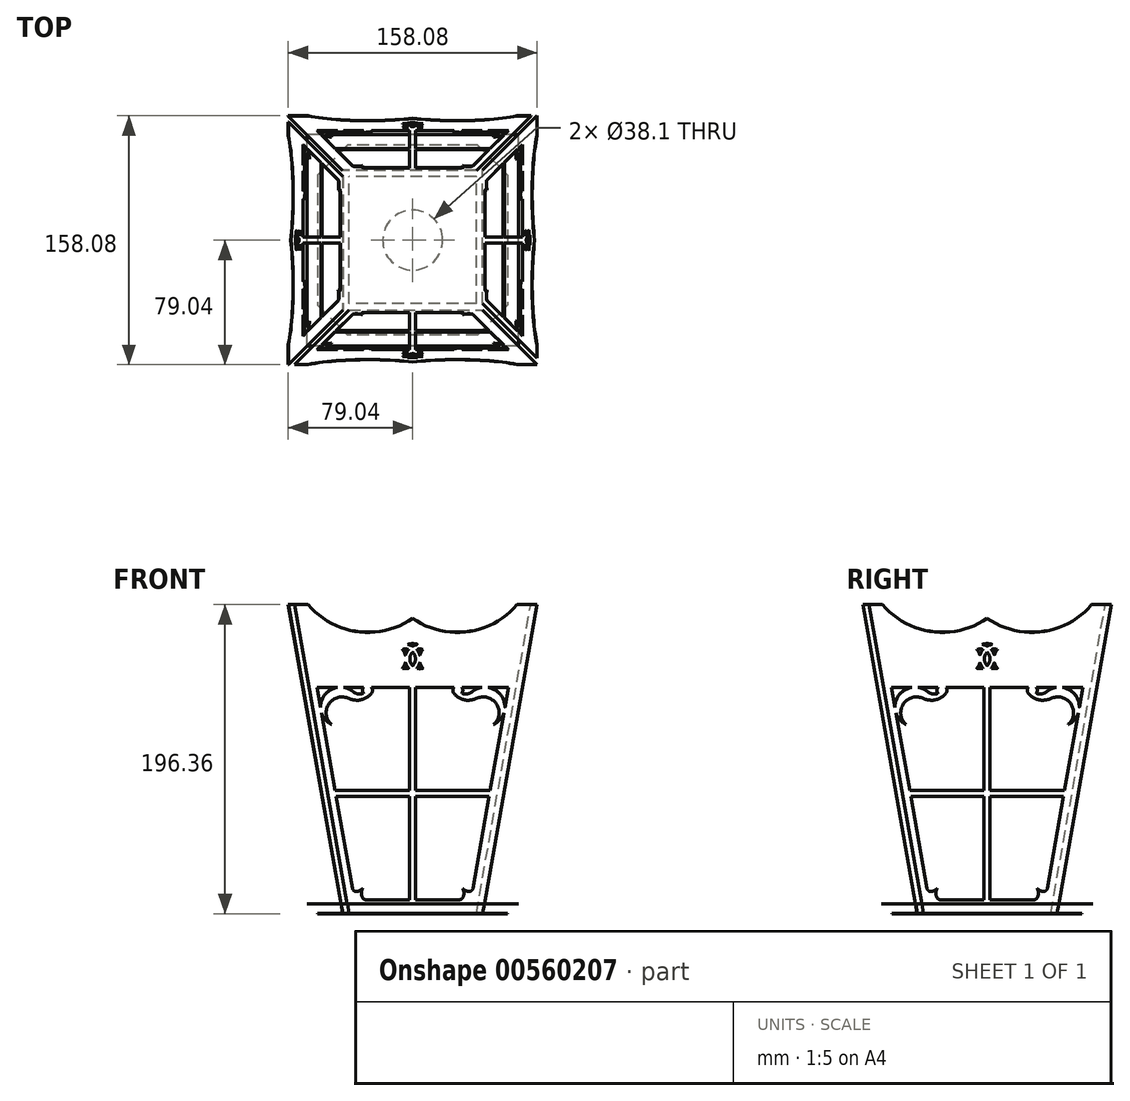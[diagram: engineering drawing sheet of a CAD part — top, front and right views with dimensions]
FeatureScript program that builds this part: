
annotation { "Feature Type Name" : "Feature", "Feature Type Description" : "" }
export const myFeature = defineFeature(function(context is Context, id is Id, definition is map)
    precondition{}
    {
        {
            assignVariable(context, id + "F0", {"name" : "wood_thickness", "anyValue" : 5 / 32});
        }
        {
            var Q0;
            Q0=qCreatedBy(makeId("Top.planeOp"),FACE);
            var sketch = newSketch(context, id + "F1", { "sketchPlane" : qUnion([Q0])});
            skLineSegment(sketch, "E0.bottom", {"start": v(41.27, 60.33) * mm, "end": v(-41.28, 60.33) * mm});
            skLineSegment(sketch, "E0.top", {"start": v(41.28, -60.32) * mm, "end": v(-41.28, -60.32) * mm});
            skLineSegment(sketch, "E0.left", {"start": v(60.32, 41.28) * mm, "end": v(60.32, -41.27) * mm});
            skLineSegment(sketch, "E0.right", {"start": v(-60.32, 41.28) * mm, "end": v(-60.32, -41.27) * mm});
            skPoint(sketch, "E0.middle", {"position": v(0, 0) * mm});
            skLineSegment(sketch, "E1", {"start": v(-41.28, 60.33) * mm, "end": v(-60.33, 41.28) * mm});
            skLineSegment(sketch, "E2", {"start": v(-60.33, -41.28) * mm, "end": v(-41.27, -60.33) * mm});
            skLineSegment(sketch, "E3", {"start": v(41.28, -60.32) * mm, "end": v(60.33, -41.27) * mm});
            skLineSegment(sketch, "E4", {"start": v(41.27, 60.33) * mm, "end": v(60.33, 41.28) * mm});
            skPoint(sketch, "E5.orphan", {"position": v(-60.32, 60.32) * mm});
            skPoint(sketch, "E6.orphan", {"position": v(60.32, 60.32) * mm});
            skPoint(sketch, "E7.orphan", {"position": v(60.32, -60.32) * mm});
            skPoint(sketch, "E8.orphan", {"position": v(-60.32, -60.32) * mm});
            skCircle(sketch, "E9", {"center": v(0, 0) * mm, "radius": 19.05 * mm});
            skLineSegment(sketch, "E10.bottom", {"start": v(44.45, -44.45) * mm, "end": v(-44.45, -44.45) * mm, "construction": true});
            skLineSegment(sketch, "E10.top", {"start": v(44.45, 44.45) * mm, "end": v(-44.45, 44.45) * mm, "construction": true});
            skLineSegment(sketch, "E10.left", {"start": v(44.45, 44.45) * mm, "end": v(44.45, -44.45) * mm, "construction": true});
            skLineSegment(sketch, "E10.right", {"start": v(-44.45, 44.45) * mm, "end": v(-44.45, -44.45) * mm, "construction": true});
            skCircle(sketch, "E11", {"center": v(0, 0) * mm, "radius": 50.8 * mm, "construction": true});
            skSolve(sketch);
        }
        {
            var Q0;
            Q0=makeQuery(id+"F1.imprint","IMPRINT",FACE,{"disambiguationData":[TD([[makeQuery(id+"F1.imprint","IMPRINT",EDGE,{"derivedFrom":sQuery(id+"F1.wireOp",EDGE,"E0.bottom")}),1.0]])]});
            extrude(context, id + "F2", {"entities" : qUnion([Q0]), "oppositeDirection" : true, "depth" : (getVariable(context, 'wood_thickness')) * mm, "offsetDistance" : 25.4 * mm});
        }
        {
            assignVariable(context, id + "F3", {"name" : "angle", "anyValue" : 10});
        }
        {
            assignVariable(context, id + "F4", {"name" : "window_height", "anyValue" : 6});
        }
        {
            var Q0;
            Q0=sQuery(id+"F1.wireOp",EDGE,"E10.bottom");
            var Q1;
            Q1=qCreatedBy(makeId("Front.planeOp"),FACE);
            cPlane(context, id + "F5", {"entities" : qUnion([Q0, Q1]), "cplaneType" : CPlaneType.LINE_ANGLE, "offset" : 25.4 * mm, "angle" : 10 * degree, "oppositeDirection" : true, "width" : 152.4 * mm, "height" : 152.4 * mm});
        }
        {
            var Q0;
            Q0=sQuery(id+"F1.wireOp",EDGE,"E10.left");
            var Q1;
            Q1=qCreatedBy(makeId("Right.planeOp"),FACE);
            cPlane(context, id + "F6", {"entities" : qUnion([Q0, Q1]), "cplaneType" : CPlaneType.LINE_ANGLE, "offset" : 25.4 * mm, "angle" : (getVariable(context, 'angle')) * degree, "oppositeDirection" : true, "width" : 152.4 * mm, "height" : 152.4 * mm});
        }
        {
            var Q0;
            Q0=qCreatedBy(makeId("Top.planeOp"),FACE);
            cPlane(context, id + "F7", {"entities" : qUnion([Q0]), "cplaneType" : CPlaneType.OFFSET, "offset" : (getVariable(context, 'window_height')) * mm, "width" : 152.4 * mm, "height" : 152.4 * mm});
        }
        {
            var Q0;
            Q0=qCreatedBy(id+"F5.planeOp",FACE);
            var sketch = newSketch(context, id + "F8", { "sketchPlane" : qUnion([Q0])});
            skLineSegment(sketch, "E12", {"start": v(44.45, 7.72) * mm, "end": v(71.32, 162.47) * mm, "construction": true});
            skLineSegment(sketch, "E13", {"start": v(71.32, 162.47) * mm, "end": v(-71.32, 162.47) * mm, "construction": true});
            skLineSegment(sketch, "E14", {"start": v(-71.32, 162.47) * mm, "end": v(-44.45, 7.72) * mm, "construction": true});
            skLineSegment(sketch, "E15", {"start": v(-44.45, 7.72) * mm, "end": v(44.45, 7.72) * mm, "construction": true});
            skPoint(sketch, "E16", {"position": v(0, 162.47) * mm});
            skPoint(sketch, "E17", {"position": v(0, 7.72) * mm});
            skLineSegment(sketch, "E18", {"start": v(40.42, 7.72) * mm, "end": v(75.01, 206.92) * mm});
            skLineSegment(sketch, "E19", {"start": v(40.42, 7.72) * mm, "end": v(-44.45, 7.72) * mm});
            skLineSegment(sketch, "E20", {"start": v(-44.45, 7.72) * mm, "end": v(-79.04, 206.92) * mm});
            skLineSegment(sketch, "E21", {"start": v(71.32, 162.47) * mm, "end": v(79.04, 206.92) * mm, "construction": true});
            skLineSegment(sketch, "E22", {"start": v(74.63, 181.52) * mm, "end": v(-74.63, 181.52) * mm, "construction": true});
            skLineSegment(sketch, "E23", {"start": v(79.04, 206.92) * mm, "end": v(66.34, 206.92) * mm, "construction": true});
            skLineSegment(sketch, "E24", {"start": v(-79.04, 206.92) * mm, "end": v(-66.34, 206.92) * mm});
            skArc(sketch, "E25", {"start": v(0, 198.03) * mm, "mid": v(34.9, 189.58) * mm, "end": v(66.34, 206.92) * mm});
            skArc(sketch, "E26", {"start": v(-66.34, 206.92) * mm, "mid": v(-34.9, 189.58) * mm, "end": v(0, 198.03) * mm});
            skLineSegment(sketch, "E27", {"start": v(75.01, 206.92) * mm, "end": v(66.34, 206.92) * mm});
            skLineSegment(sketch, "E28", {"start": v(79.04, 206.92) * mm, "end": v(74.1, 207.78) * mm, "construction": true});
            skLineSegment(sketch, "E29", {"start": v(29.6, 16.6) * mm, "end": v(1.9, 16.6) * mm});
            skPoint(sketch, "E30", {"position": v(0, 16.6) * mm});
            skLineSegment(sketch, "E31", {"start": v(-60.76, 153.58) * mm, "end": v(-47.74, 153.58) * mm});
            skLineSegment(sketch, "E32", {"start": v(60.76, 153.58) * mm, "end": v(58.53, 140.75) * mm});
            skLineSegment(sketch, "E33", {"start": v(60.76, 153.58) * mm, "end": v(-36.97, 16.6) * mm, "construction": true});
            skLineSegment(sketch, "E34", {"start": v(-60.76, 153.58) * mm, "end": v(36.97, 16.6) * mm, "construction": true});
            skLineSegment(sketch, "E35", {"start": v(0, 153.58) * mm, "end": v(0, 16.6) * mm, "construction": true});
            skLineSegment(sketch, "E36", {"start": v(48.86, 85.1) * mm, "end": v(-48.86, 85.1) * mm, "construction": true});
            skArc(sketch, "E37", {"start": v(-31.87, 18) * mm, "mid": v(-30.94, 16.99) * mm, "end": v(-29.6, 16.6) * mm});
            skArc(sketch, "E38", {"start": v(-31.8, 23.85) * mm, "mid": v(-32.55, 20.93) * mm, "end": v(-31.87, 18) * mm});
            skLineSegment(sketch, "E39", {"start": v(-31.8, 23.85) * mm, "end": v(-35.66, 16.6) * mm, "construction": true});
            skArc(sketch, "E40", {"start": v(-35.28, 21.93) * mm, "mid": v(-33.4, 22.61) * mm, "end": v(-31.8, 23.85) * mm});
            skLineSegment(sketch, "E41", {"start": v(-31.8, 23.85) * mm, "end": v(-37.22, 18.04) * mm, "construction": true});
            skArc(sketch, "E42", {"start": v(-38.25, 24) * mm, "mid": v(-37.2, 22.35) * mm, "end": v(-35.28, 21.93) * mm});
            skLineSegment(sketch, "E43.trimOffspring", {"start": v(-38.25, 24) * mm, "end": v(-48.53, 83.19) * mm});
            skArc(sketch, "E44", {"start": v(29.6, 16.6) * mm, "mid": v(30.94, 16.99) * mm, "end": v(31.87, 18) * mm});
            skArc(sketch, "E45", {"start": v(31.87, 18) * mm, "mid": v(32.55, 20.93) * mm, "end": v(31.8, 23.85) * mm});
            skArc(sketch, "E46", {"start": v(31.8, 23.85) * mm, "mid": v(33.4, 22.61) * mm, "end": v(35.28, 21.93) * mm});
            skArc(sketch, "E47", {"start": v(35.28, 21.93) * mm, "mid": v(37.2, 22.35) * mm, "end": v(38.25, 24) * mm});
            skLineSegment(sketch, "E48", {"start": v(31.8, 23.85) * mm, "end": v(34.55, 18.69) * mm, "construction": true});
            skLineSegment(sketch, "E49", {"start": v(31.8, 23.85) * mm, "end": v(35.1, 20.32) * mm, "construction": true});
            skLineSegment(sketch, "E50", {"start": v(1.9, 153.58) * mm, "end": v(1.9, 87) * mm});
            skLineSegment(sketch, "E51", {"start": v(-1.9, 153.58) * mm, "end": v(-1.9, 87) * mm});
            skLineSegment(sketch, "E52", {"start": v(1.9, 112.49) * mm, "end": v(-1.9, 112.49) * mm, "construction": true});
            skPoint(sketch, "E53", {"position": v(0, 112.49) * mm});
            skLineSegment(sketch, "E54", {"start": v(49.2, 87) * mm, "end": v(1.9, 87) * mm});
            skLineSegment(sketch, "E55", {"start": v(-48.53, 83.19) * mm, "end": v(-1.9, 83.19) * mm});
            skLineSegment(sketch, "E56", {"start": v(26.8, 87) * mm, "end": v(26.8, 83.19) * mm, "construction": true});
            skPoint(sketch, "E57", {"position": v(26.8, 85.1) * mm});
            skLineSegment(sketch, "E58", {"start": v(60.76, 153.58) * mm, "end": v(0, 102.47) * mm, "construction": true});
            skLineSegment(sketch, "E59", {"start": v(0, 102.47) * mm, "end": v(-60.76, 153.58) * mm, "construction": true});
            skLineSegment(sketch, "E60", {"start": v(-37.33, 153.58) * mm, "end": v(-56.75, 130.5) * mm, "construction": true});
            skPoint(sketch, "E61", {"position": v(-47.04, 142.04) * mm});
            skArc(sketch, "E62", {"start": v(51.47, 129.65) * mm, "mid": v(55.4, 132.68) * mm, "end": v(57.88, 137) * mm});
            skPoint(sketch, "E63", {"position": v(47.74, 153.58) * mm});
            skPoint(sketch, "E64", {"position": v(43.93, 153.58) * mm});
            skArc(sketch, "E65", {"start": v(37.58, 150.67) * mm, "mid": v(34.53, 149.3) * mm, "end": v(31.22, 149.77) * mm});
            skArc(sketch, "E66", {"start": v(51.47, 129.65) * mm, "mid": v(53.23, 142.87) * mm, "end": v(40.38, 146.44) * mm});
            skLineSegment(sketch, "E67", {"start": v(51.47, 129.65) * mm, "end": v(37.58, 150.67) * mm, "construction": true});
            skLineSegment(sketch, "E68", {"start": v(51.47, 129.65) * mm, "end": v(48.2, 128.02) * mm, "construction": true});
            skLineSegment(sketch, "E69", {"start": v(51.47, 129.65) * mm, "end": v(49.55, 127.95) * mm, "construction": true});
            skArc(sketch, "E70", {"start": v(26.15, 153.58) * mm, "mid": v(25.51, 151.67) * mm, "end": v(26.15, 149.77) * mm});
            skArc(sketch, "E71.trimOffspring", {"start": v(26.15, 149.77) * mm, "mid": v(32.68, 145.6) * mm, "end": v(40.38, 146.44) * mm});
            skArc(sketch, "E72.trimOffspring", {"start": v(31.22, 149.77) * mm, "mid": v(31.86, 151.67) * mm, "end": v(31.22, 153.58) * mm});
            skLineSegment(sketch, "E73", {"start": v(31.22, 153.58) * mm, "end": v(26.15, 149.77) * mm, "construction": true});
            skLineSegment(sketch, "E74", {"start": v(26.15, 153.58) * mm, "end": v(31.22, 149.77) * mm, "construction": true});
            skPoint(sketch, "E75", {"position": v(58.53, 140.75) * mm});
            skPoint(sketch, "E76", {"position": v(57.88, 137) * mm});
            skArc(sketch, "E77.trimOffspring", {"start": v(58.53, 140.75) * mm, "mid": v(55.55, 149.2) * mm, "end": v(47.74, 153.58) * mm});
            skLineSegment(sketch, "E78.trimOffspring", {"start": v(57.88, 137) * mm, "end": v(49.2, 87) * mm});
            skArc(sketch, "E79.trimOffspring", {"start": v(43.93, 153.58) * mm, "mid": v(40.55, 152.57) * mm, "end": v(37.58, 150.67) * mm});
            skLineSegment(sketch, "E80.trimOffspring", {"start": v(47.74, 153.58) * mm, "end": v(60.76, 153.58) * mm});
            skArc(sketch, "E81.MirrorCS", {"start": v(-26.15, 153.58) * mm, "mid": v(-25.51, 151.67) * mm, "end": v(-26.15, 149.77) * mm});
            skArc(sketch, "E82.MirrorCS", {"start": v(-31.22, 149.77) * mm, "mid": v(-31.86, 151.67) * mm, "end": v(-31.22, 153.58) * mm});
            skArc(sketch, "E83.MirrorCS", {"start": v(-37.58, 150.67) * mm, "mid": v(-34.53, 149.3) * mm, "end": v(-31.22, 149.77) * mm});
            skArc(sketch, "E84.MirrorCS", {"start": v(-26.15, 149.77) * mm, "mid": v(-32.68, 145.6) * mm, "end": v(-40.38, 146.44) * mm});
            skArc(sketch, "E85.MirrorCS", {"start": v(-43.93, 153.58) * mm, "mid": v(-40.55, 152.57) * mm, "end": v(-37.58, 150.67) * mm});
            skArc(sketch, "E86.MirrorCS", {"start": v(-51.47, 129.65) * mm, "mid": v(-55.4, 132.68) * mm, "end": v(-57.88, 137) * mm});
            skArc(sketch, "E87.MirrorCS", {"start": v(-51.47, 129.65) * mm, "mid": v(-53.23, 142.87) * mm, "end": v(-40.38, 146.44) * mm});
            skArc(sketch, "E88.MirrorCS", {"start": v(-58.53, 140.75) * mm, "mid": v(-55.55, 149.2) * mm, "end": v(-47.74, 153.58) * mm});
            skLineSegment(sketch, "E89.trimOffspring", {"start": v(31.22, 153.58) * mm, "end": v(43.93, 153.58) * mm});
            skLineSegment(sketch, "E90.trimOffspring", {"start": v(-26.15, 153.58) * mm, "end": v(-1.9, 153.58) * mm});
            skLineSegment(sketch, "E91.trimOffspring", {"start": v(-43.93, 153.58) * mm, "end": v(-31.22, 153.58) * mm});
            skLineSegment(sketch, "E92.trimOffspring", {"start": v(-58.53, 140.75) * mm, "end": v(-60.76, 153.58) * mm});
            skLineSegment(sketch, "E93.trimOffspring", {"start": v(-1.9, 87) * mm, "end": v(-49.2, 87) * mm});
            skLineSegment(sketch, "E94.trimOffspring", {"start": v(1.9, 83.19) * mm, "end": v(1.9, 16.6) * mm});
            skLineSegment(sketch, "E95.trimOffspring", {"start": v(1.9, 83.19) * mm, "end": v(48.53, 83.19) * mm});
            skLineSegment(sketch, "E96.trimOffspring", {"start": v(-1.9, 83.19) * mm, "end": v(-1.9, 16.6) * mm});
            skLineSegment(sketch, "E97.trimOffspring", {"start": v(48.53, 83.19) * mm, "end": v(38.25, 24) * mm});
            skLineSegment(sketch, "E98.trimOffspring", {"start": v(-49.2, 87) * mm, "end": v(-57.88, 137) * mm});
            skLineSegment(sketch, "E99.trimOffspring", {"start": v(-1.9, 16.6) * mm, "end": v(-29.6, 16.6) * mm});
            skLineSegment(sketch, "E100.trimOffspring", {"start": v(1.9, 153.58) * mm, "end": v(26.15, 153.58) * mm});
            skLineSegment(sketch, "E101", {"start": v(0, 162.47) * mm, "end": v(0, 181.52) * mm, "construction": true});
            skPoint(sketch, "E102", {"position": v(0, 172) * mm});
            skArc(sketch, "E103", {"start": v(0, 180.2) * mm, "mid": v(-1.54, 180.89) * mm, "end": v(-3.17, 181.29) * mm});
            skArc(sketch, "E104", {"start": v(-2.62, 178.04) * mm, "mid": v(-3.82, 176.22) * mm, "end": v(-4.57, 174.16) * mm});
            skLineSegment(sketch, "E105", {"start": v(4.57, 172) * mm, "end": v(-4.57, 172) * mm, "construction": true});
            skArc(sketch, "E106", {"start": v(0, 176.4) * mm, "mid": v(-1.78, 172) * mm, "end": v(0, 167.59) * mm});
            skArc(sketch, "E107", {"start": v(-2.62, 178.04) * mm, "mid": v(-4.57, 178.34) * mm, "end": v(-6.52, 178.04) * mm});
            skArc(sketch, "E108", {"start": v(-4.57, 174.16) * mm, "mid": v(-5.32, 176.22) * mm, "end": v(-6.52, 178.04) * mm});
            skArc(sketch, "E109", {"start": v(6.52, 178.04) * mm, "mid": v(5.32, 176.22) * mm, "end": v(4.57, 174.16) * mm});
            skArc(sketch, "E110", {"start": v(3.18, 181.29) * mm, "mid": v(0, 181.82) * mm, "end": v(-3.17, 181.29) * mm});
            skArc(sketch, "E111.trimOffspring", {"start": v(6.52, 178.04) * mm, "mid": v(4.57, 178.34) * mm, "end": v(2.62, 178.04) * mm});
            skArc(sketch, "E112.trimOffspring", {"start": v(3.18, 181.29) * mm, "mid": v(1.54, 180.89) * mm, "end": v(0, 180.2) * mm});
            skArc(sketch, "E113.trimOffspring", {"start": v(2.62, 165.95) * mm, "mid": v(3.82, 167.77) * mm, "end": v(4.57, 169.82) * mm});
            skArc(sketch, "E114.trimOffspring", {"start": v(2.62, 165.95) * mm, "mid": v(4.57, 165.64) * mm, "end": v(6.52, 165.95) * mm});
            skArc(sketch, "E115.trimOffspring", {"start": v(4.57, 169.82) * mm, "mid": v(5.32, 167.77) * mm, "end": v(6.52, 165.95) * mm});
            skArc(sketch, "E116.trimOffspring", {"start": v(4.57, 174.16) * mm, "mid": v(3.82, 176.22) * mm, "end": v(2.62, 178.04) * mm});
            skArc(sketch, "E117.trimOffspring", {"start": v(0, 167.59) * mm, "mid": v(1.78, 172) * mm, "end": v(0, 176.4) * mm});
            skArc(sketch, "E118.trimOffspring", {"start": v(-4.57, 169.82) * mm, "mid": v(-3.82, 167.77) * mm, "end": v(-2.62, 165.95) * mm});
            skArc(sketch, "E119.trimOffspring", {"start": v(-6.52, 165.95) * mm, "mid": v(-5.32, 167.77) * mm, "end": v(-4.57, 169.82) * mm});
            skArc(sketch, "E120.trimOffspring", {"start": v(-6.52, 165.95) * mm, "mid": v(-4.57, 165.64) * mm, "end": v(-2.62, 165.95) * mm});
            skSolve(sketch);
        }
        {
            var Q0;
            Q0 = qSketchRegion(id + "F8", true);
            extrude(context, id + "F9", {"entities" : qUnion([Q0]), "depth" : (getVariable(context, 'wood_thickness')) * mm, "offsetDistance" : 25.4 * mm});
        }
        {
            var Q0;
            Q0=qCreatedBy(makeId("Front.planeOp"),FACE);
            var sketch = newSketch(context, id + "F10", { "sketchPlane" : qUnion([Q0])});
            skLineSegment(sketch, "E121", {"start": v(0, 0) * mm, "end": v(0, 130.04) * mm});
            skSolve(sketch);
        }
        {
            var Q0;
            Q0=makeQuery(id+"F9.opExtrude","SWEPT_BODY",BODY,{"disambiguationData":[OSD([sQuery(id+"F8.wireOp",EDGE,"E18"),sQuery(id+"F8.wireOp",EDGE,"E19"),sQuery(id+"F8.wireOp",EDGE,"E20"),sQuery(id+"F8.wireOp",EDGE,"E24"),sQuery(id+"F8.wireOp",EDGE,"E25"),sQuery(id+"F8.wireOp",EDGE,"E26"),sQuery(id+"F8.wireOp",EDGE,"E27"),sQuery(id+"F8.wireOp",EDGE,"E29"),sQuery(id+"F8.wireOp",EDGE,"E31"),sQuery(id+"F8.wireOp",EDGE,"E32"),sQuery(id+"F8.wireOp",EDGE,"E37"),sQuery(id+"F8.wireOp",EDGE,"E38"),sQuery(id+"F8.wireOp",EDGE,"E40"),sQuery(id+"F8.wireOp",EDGE,"E42"),sQuery(id+"F8.wireOp",EDGE,"E43.trimOffspring"),sQuery(id+"F8.wireOp",EDGE,"E44"),sQuery(id+"F8.wireOp",EDGE,"E45"),sQuery(id+"F8.wireOp",EDGE,"E46"),sQuery(id+"F8.wireOp",EDGE,"E47"),sQuery(id+"F8.wireOp",EDGE,"E50"),sQuery(id+"F8.wireOp",EDGE,"E51"),sQuery(id+"F8.wireOp",EDGE,"E54"),sQuery(id+"F8.wireOp",EDGE,"E55"),sQuery(id+"F8.wireOp",EDGE,"E62"),sQuery(id+"F8.wireOp",EDGE,"E65"),sQuery(id+"F8.wireOp",EDGE,"E66"),sQuery(id+"F8.wireOp",EDGE,"E70"),sQuery(id+"F8.wireOp",EDGE,"E71.trimOffspring"),sQuery(id+"F8.wireOp",EDGE,"E72.trimOffspring"),sQuery(id+"F8.wireOp",EDGE,"E77.trimOffspring"),sQuery(id+"F8.wireOp",EDGE,"E78.trimOffspring"),sQuery(id+"F8.wireOp",EDGE,"E79.trimOffspring"),sQuery(id+"F8.wireOp",EDGE,"E80.trimOffspring"),sQuery(id+"F8.wireOp",EDGE,"E81.MirrorCS"),sQuery(id+"F8.wireOp",EDGE,"E82.MirrorCS"),sQuery(id+"F8.wireOp",EDGE,"E83.MirrorCS"),sQuery(id+"F8.wireOp",EDGE,"E84.MirrorCS"),sQuery(id+"F8.wireOp",EDGE,"E85.MirrorCS"),sQuery(id+"F8.wireOp",EDGE,"E86.MirrorCS"),sQuery(id+"F8.wireOp",EDGE,"E87.MirrorCS"),sQuery(id+"F8.wireOp",EDGE,"E88.MirrorCS"),sQuery(id+"F8.wireOp",EDGE,"E89.trimOffspring"),sQuery(id+"F8.wireOp",EDGE,"E90.trimOffspring"),sQuery(id+"F8.wireOp",EDGE,"E91.trimOffspring"),sQuery(id+"F8.wireOp",EDGE,"E92.trimOffspring"),sQuery(id+"F8.wireOp",EDGE,"E93.trimOffspring"),sQuery(id+"F8.wireOp",EDGE,"E94.trimOffspring"),sQuery(id+"F8.wireOp",EDGE,"E95.trimOffspring"),sQuery(id+"F8.wireOp",EDGE,"E96.trimOffspring"),sQuery(id+"F8.wireOp",EDGE,"E97.trimOffspring"),sQuery(id+"F8.wireOp",EDGE,"E98.trimOffspring"),sQuery(id+"F8.wireOp",EDGE,"E99.trimOffspring"),sQuery(id+"F8.wireOp",EDGE,"E100.trimOffspring"),sQuery(id+"F8.wireOp",EDGE,"E103"),sQuery(id+"F8.wireOp",EDGE,"E104"),sQuery(id+"F8.wireOp",EDGE,"E106"),sQuery(id+"F8.wireOp",EDGE,"E107"),sQuery(id+"F8.wireOp",EDGE,"E108"),sQuery(id+"F8.wireOp",EDGE,"E109"),sQuery(id+"F8.wireOp",EDGE,"E110"),sQuery(id+"F8.wireOp",EDGE,"E111.trimOffspring"),sQuery(id+"F8.wireOp",EDGE,"E112.trimOffspring"),sQuery(id+"F8.wireOp",EDGE,"E113.trimOffspring"),sQuery(id+"F8.wireOp",EDGE,"E114.trimOffspring"),sQuery(id+"F8.wireOp",EDGE,"E115.trimOffspring"),sQuery(id+"F8.wireOp",EDGE,"E116.trimOffspring"),sQuery(id+"F8.wireOp",EDGE,"E117.trimOffspring"),sQuery(id+"F8.wireOp",EDGE,"E118.trimOffspring"),sQuery(id+"F8.wireOp",EDGE,"E119.trimOffspring"),sQuery(id+"F8.wireOp",EDGE,"E120.trimOffspring")])]});
            var Q1;
            Q1=sQuery(id+"F10.wireOp",EDGE,"E121");
            circularPattern(context, id + "F11", {"entities" : qUnion([Q0]), "axis" : qUnion([Q1]), "angle" : 360 * degree, "instanceCount" : 4, "equalSpace" : true});
        }
        {
            var Q0;
            Q0=qCreatedBy(makeId("Top.planeOp"),FACE);
            var sketch = newSketch(context, id + "F12", { "sketchPlane" : qUnion([Q0])});
            skLineSegment(sketch, "E122.0", {"start": v(40.54, -40.42) * mm, "end": v(40.54, 44.45) * mm, "construction": true});
            skLineSegment(sketch, "E123.0", {"start": v(-40.42, -40.54) * mm, "end": v(44.45, -40.54) * mm, "construction": true});
            skLineSegment(sketch, "E124.0", {"start": v(-40.54, 40.42) * mm, "end": v(-40.54, -44.45) * mm, "construction": true});
            skLineSegment(sketch, "E125.0", {"start": v(40.42, 40.54) * mm, "end": v(-44.45, 40.54) * mm, "construction": true});
            skCircle(sketch, "E126.0", {"center": v(0, 0) * mm, "radius": 19.05 * mm});
            skLineSegment(sketch, "E127.bottom", {"start": v(40.54, -40.42) * mm, "end": v(-40.54, -40.42) * mm});
            skLineSegment(sketch, "E127.top", {"start": v(40.54, 40.42) * mm, "end": v(-40.54, 40.42) * mm});
            skLineSegment(sketch, "E127.left", {"start": v(40.54, -40.42) * mm, "end": v(40.54, 40.42) * mm});
            skLineSegment(sketch, "E127.right", {"start": v(-40.54, -40.42) * mm, "end": v(-40.54, 40.42) * mm});
            skSolve(sketch);
        }
        {
            var Q0;
            Q0 = qSketchRegion(id + "F12", true);
            extrude(context, id + "F13", {"entities" : qUnion([Q0]), "depth" : (getVariable(context, 'wood_thickness')) * mm, "offsetDistance" : 25.4 * mm});
        }
        {
            var Q0;
            Q0=qCreatedBy(id+"F7.planeOp",FACE);
            var sketch = newSketch(context, id + "F14", { "sketchPlane" : qUnion([Q0])});
            skEllipticalArc(sketch, "E128.0.1", {});
            skLineSegment(sketch, "E129", {"start": v(71.2, -67.3) * mm, "end": v(-67.17, -67.3) * mm, "construction": true});
            skPoint(sketch, "E130", {"position": v(67.3, -67.3) * mm});
            skLineSegment(sketch, "E131.bottom", {"start": v(67.3, -67.3) * mm, "end": v(-67.17, -67.3) * mm});
            skLineSegment(sketch, "E131.top", {"start": v(67.3, 67.17) * mm, "end": v(-67.17, 67.17) * mm});
            skLineSegment(sketch, "E131.left", {"start": v(67.3, -67.3) * mm, "end": v(67.3, 67.17) * mm});
            skLineSegment(sketch, "E131.right", {"start": v(-67.17, -67.3) * mm, "end": v(-67.17, 67.17) * mm});
            const initialGuessF14  = {"E128.0.1": [0.028317928011268922, -0.08064863610386974, -1, 0, 0.04954652119524263, 0.008603663115289824, 3.8375824471921143, 5.320773034347993]};
            skSetInitialGuess(sketch, initialGuessF14);
            skSolve(sketch);
        }
        {
            var Q0;
            Q0 = qSketchRegion(id + "F14", true);
            extrude(context, id + "F15", {"entities" : qUnion([Q0]), "depth" : (getVariable(context, 'wood_thickness')) * mm, "offsetDistance" : 25.4 * mm});
        }
    });
